# Revit family: Legrand_Practibox³_8_and_12_modules_white_door
name_source: partatom
category: Equipement électrique
revit_build: Autodesk Revit 2018 (Build: 20170223_1515(x64)
units: mm (PartAtom-declared; Revit-internal decimal feet)

## family parameters
Basée sur le plan de construction = Non
Configuration du panneau = Deux colonnes, circuits au sein
Cote de connecteur circulaire = Utiliser le diamètre
Couper avec des vides une fois chargée = Non
Numéro OmniClass = 23.80.30.11.17
Partagée = Non
Point de calcul de pièce = Non
Titre OmniClass = Distribution Boards and Control Panels
Toujours verticalement = Oui
Type d'élément = Tableau de raccordement

## types (8) — shared parameters
Fabricant = Legrand
General Conditions of Use = https://export.legrand.com
Modèle = Practibox³
URL = www.legrand.com
transparent door = Non
white door = Oui

## per-type parameters (varying)
| type | 401711 | 401712 | 401713 | 401714 | 401761 | 401762 | 401763 | 401764 | Terminal block E | Terminal block N | depth | height | width |
| Practibox³ 1x8 modules 401711 | Oui | Non | Non | Non | Non | Non | Non | Non | terminal block 8 holes |  | 100 mm  [stored 0.328084 ft] | 208 mm  [stored 0.682415 ft] | 286 mm |
| Practibox³ 1x12 modules 401712 | Non | Oui | Non | Non | Non | Non | Non | Non | terminal block 13 holes |  | 100 mm  [stored 0.328084 ft] | 246 mm  [stored 0.807087 ft] | 359 mm  [stored 1.17782 ft] |
| Practibox³ 2x12 modules 401713 | Non | Non | Oui | Non | Non | Non | Non | Non | terminal block 17 holes |  | 105 mm  [stored 0.344488 ft] | 396 mm  [stored 1.29921 ft] | 359 mm  [stored 1.17782 ft] |
| Practibox³ 3x12 modules 401714 | Non | Non | Non | Oui | Non | Non | Non | Non | terminal block 22 holes |  | 105 mm  [stored 0.344488 ft] | 546 mm  [stored 1.79134 ft] | 359 mm  [stored 1.17782 ft] |
| Practibox³ 1x8 modules 401761 | Non | Non | Non | Non | Oui | Non | Non | Non | terminal block 8 holes | terminal block 8 holes | 100 mm  [stored 0.328084 ft] | 208 mm  [stored 0.682415 ft] | 286 mm |
| Practibox³ 1x12 modules 401762 | Non | Non | Non | Non | Non | Oui | Non | Non | terminal block 13 holes | terminal block 8 holes | 100 mm  [stored 0.328084 ft] | 246 mm  [stored 0.807087 ft] | 359 mm  [stored 1.17782 ft] |
| Practibox³ 2x12 modules 401763 | Non | Non | Non | Non | Non | Non | Oui | Non | terminal block 17 holes | terminal block 2x8 holes | 105 mm  [stored 0.344488 ft] | 396 mm  [stored 1.29921 ft] | 359 mm  [stored 1.17782 ft] |
| Practibox³ 3x12 modules 401764 | Non | Non | Non | Non | Non | Non | Non | Oui | terminal block 22 holes | terminal block 3x8 holes | 105 mm  [stored 0.344488 ft] | 546 mm  [stored 1.79134 ft] | 359 mm  [stored 1.17782 ft] |

note: [stored X ft] marks values corroborated as IEEE doubles in the binary element streams (Revit-internal decimal feet)
